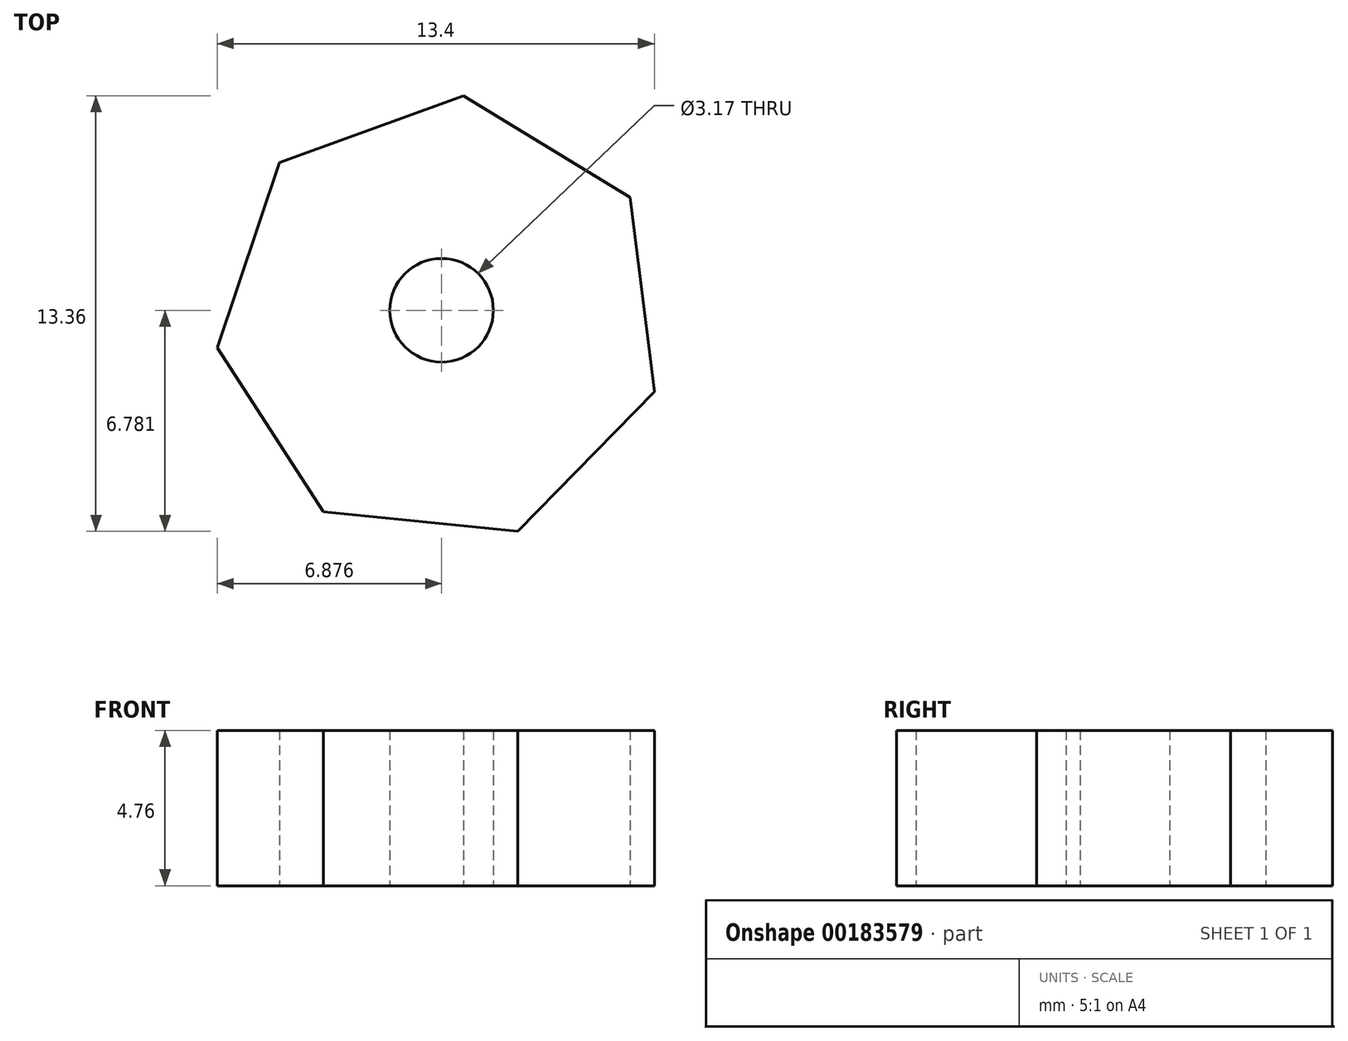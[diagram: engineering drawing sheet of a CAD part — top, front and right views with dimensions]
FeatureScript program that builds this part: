
annotation { "Feature Type Name" : "Feature", "Feature Type Description" : "" }
export const myFeature = defineFeature(function(context is Context, id is Id, definition is map)
    precondition{}
    {
        {
            var Q0;
            Q0=qCreatedBy(makeId("Top.planeOp"),FACE);
            var sketch = newSketch(context, id + "F0", { "sketchPlane" : qUnion([Q0])});
            skCircle(sketch, "E0.cCircle", {"center": v(-40.03, 18.96) * mm, "radius": 6.22 * mm, "construction": true});
            skLineSegment(sketch, "E0.0", {"start": v(-33.48, 16.76) * mm, "end": v(-37.66, 12.47) * mm});
            skLineSegment(sketch, "E0.1", {"start": v(-37.66, 12.47) * mm, "end": v(-43.62, 13.07) * mm});
            skLineSegment(sketch, "E0.2", {"start": v(-43.62, 13.07) * mm, "end": v(-46.88, 18.1) * mm});
            skLineSegment(sketch, "E0.3", {"start": v(-46.88, 18.1) * mm, "end": v(-44.97, 23.78) * mm});
            skLineSegment(sketch, "E0.4", {"start": v(-44.97, 23.78) * mm, "end": v(-39.34, 25.83) * mm});
            skLineSegment(sketch, "E0.5", {"start": v(-39.34, 25.83) * mm, "end": v(-34.23, 22.7) * mm});
            skLineSegment(sketch, "E0.6", {"start": v(-34.23, 22.7) * mm, "end": v(-33.48, 16.76) * mm});
            skPoint(sketch, "E0.0.midPoint", {"position": v(-35.57, 14.62) * mm});
            skSolve(sketch);
        }
        {
            var Q0;
            Q0=qCreatedBy(makeId("Top.planeOp"),FACE);
            var sketch = newSketch(context, id + "F1", { "sketchPlane" : qUnion([Q0])});
            skSolve(sketch);
        }
        {
            var Q0;
            Q0 = qSketchRegion(id + "F1", true);
            var Q1;
            Q1=makeQuery(id+"F0.imprint","IMPRINT",FACE,{"disambiguationData":[TD([[makeQuery(id+"F0.imprint","IMPRINT",EDGE,{"derivedFrom":sQuery(id+"F0.wireOp",EDGE,"E0.0")}),-1.0]])]});
            extrude(context, id + "F2", {"entities" : qUnion([Q0, Q1]), "depth" : 4.76 * mm});
        }
        {
            var Q0;
            Q0=qCreatedBy(makeId("Top.planeOp"),FACE);
            var sketch = newSketch(context, id + "F3", { "sketchPlane" : qUnion([Q0])});
            skCircle(sketch, "E1", {"center": v(-40, 19.25) * mm, "radius": 1.59 * mm});
            skSolve(sketch);
        }
        {
            var Q0;
            Q0 = qSketchRegion(id + "F3", true);
            extrude(context, id + "F4", {"entities" : qUnion([Q0]), "operationType" : NewBodyOperationType.REMOVE, "depth" : 18.03 * mm});
        }
    });
